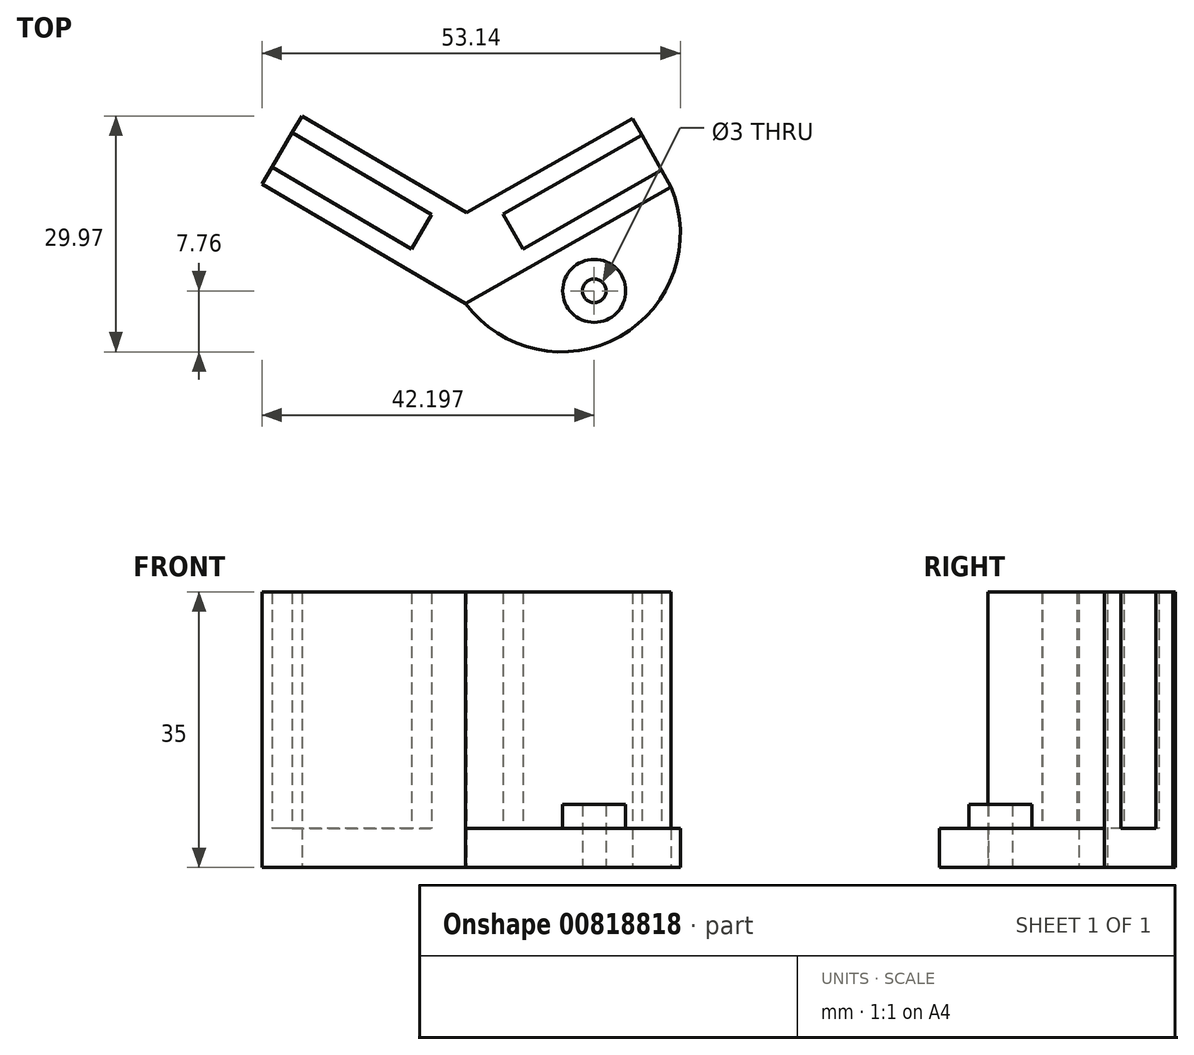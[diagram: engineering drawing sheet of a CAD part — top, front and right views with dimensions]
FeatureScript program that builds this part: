
annotation { "Feature Type Name" : "Feature", "Feature Type Description" : "" }
export const myFeature = defineFeature(function(context is Context, id is Id, definition is map)
    precondition{}
    {
        {
            var Q0;
            Q0=qCreatedBy(makeId("Top.planeOp"),FACE);
            var sketch = newSketch(context, id + "F0", { "sketchPlane" : qUnion([Q0])});
            skCircle(sketch, "E0.cCircle", {"center": v(0, 0) * mm, "radius": 30 * mm, "construction": true});
            skLineSegment(sketch, "E0.0", {"start": v(-26.1, -14.8) * mm, "end": v(-25.86, 15.2) * mm});
            skLineSegment(sketch, "E0.1", {"start": v(-25.86, 15.2) * mm, "end": v(0.23, 30) * mm});
            skLineSegment(sketch, "E0.2", {"start": v(0.23, 30) * mm, "end": v(26.1, 14.8) * mm});
            skLineSegment(sketch, "E0.3", {"start": v(26.1, 14.8) * mm, "end": v(25.86, -15.2) * mm});
            skLineSegment(sketch, "E0.4", {"start": v(25.86, -15.2) * mm, "end": v(-0.23, -30) * mm});
            skLineSegment(sketch, "E0.5", {"start": v(-0.23, -30) * mm, "end": v(-26.1, -14.8) * mm});
            skLineSegment(sketch, "E1", {"start": v(66.66, -58.3) * mm, "end": v(69.7, -53.13) * mm});
            skLineSegment(sketch, "E2.0", {"start": v(-0.14, -18.45) * mm, "end": v(-21.03, -6.18) * mm});
            skLineSegment(sketch, "E2.1", {"start": v(20.93, -6.5) * mm, "end": v(-0.14, -18.45) * mm});
            skLineSegment(sketch, "E3.0", {"start": v(-0.21, -27.17) * mm, "end": v(-24.86, -12.68) * mm});
            skLineSegment(sketch, "E3.1", {"start": v(24.65, -13.07) * mm, "end": v(-0.21, -27.17) * mm});
            skLineSegment(sketch, "E4", {"start": v(20.93, -6.5) * mm, "end": v(25.86, -15.2) * mm});
            skLineSegment(sketch, "E5", {"start": v(-21.03, -6.18) * mm, "end": v(-26.1, -14.8) * mm});
            skArc(sketch, "E6", {"start": v(-0.23, -30) * mm, "mid": v(19.38, -34.18) * mm, "end": v(25.86, -15.2) * mm});
            skLineSegment(sketch, "E7", {"start": v(19.38, -34.18) * mm, "end": v(12.81, -22.6) * mm});
            skCircle(sketch, "E8", {"center": v(16.1, -28.4) * mm, "radius": 4 * mm});
            skLineSegment(sketch, "E9", {"start": v(4.53, -18.62) * mm, "end": v(7.05, -23.05) * mm});
            skLineSegment(sketch, "E10", {"start": v(-22.27, -8.29) * mm, "end": v(-4.54, -18.7) * mm});
            skLineSegment(sketch, "E11", {"start": v(-4.54, -18.7) * mm, "end": v(-7.13, -23.1) * mm});
            skLineSegment(sketch, "E12", {"start": v(4.53, -18.62) * mm, "end": v(22.14, -8.63) * mm});
            skCircle(sketch, "E13", {"center": v(16.1, -28.4) * mm, "radius": 1.5 * mm});
            skSolve(sketch);
        }
        {
            var Q0;
            {var subQ7=sQuery(id+"F0.wireOp",EDGE,"E2.0");Q0=makeQuery(id+"F0.imprint","IMPRINT",FACE,{"disambiguationData":[TD([[makeQuery(id+"F0.imprint","IMPRINT",EDGE,{"derivedFrom":subQ7}),1.0]])]});}
            var Q1;
            {var subQ0=sQuery(id+"F0.wireOp",EDGE,"E0.5");Q1=makeQuery(id+"F0.imprint","IMPRINT",FACE,{"disambiguationData":[TD([[makeQuery(id+"F0.imprint","IMPRINT",EDGE,{"derivedFrom":subQ0}),-1.0]])]});}
            extrude(context, id + "F1", {"entities" : qUnion([Q0, Q1]), "depth" : 35 * mm, "offsetDistance" : 25 * mm});
        }
        {
            var Q0;
            {var subQ4=sQuery(id+"F0.wireOp",EDGE,"E10");Q0=makeQuery(id+"F0.imprint","IMPRINT",FACE,{"disambiguationData":[TD([[makeQuery(id+"F0.imprint","IMPRINT",EDGE,{"derivedFrom":subQ4}),-1.0]])]});}
            var Q1;
            {var subQ3=sQuery(id+"F0.wireOp",EDGE,"E9");Q1=makeQuery(id+"F0.imprint","IMPRINT",FACE,{"disambiguationData":[TD([[makeQuery(id+"F0.imprint","IMPRINT",EDGE,{"derivedFrom":subQ3}),1.0]])]});}
            extrude(context, id + "F2", {"entities" : qUnion([Q0, Q1]), "operationType" : NewBodyOperationType.ADD, "depth" : 5 * mm, "offsetDistance" : 25 * mm});
        }
        {
            var Q0;
            {var subQ0=sQuery(id+"F0.wireOp",EDGE,"E7");var subQ1=sQuery(id+"F0.wireOp",EDGE,"E6");var subQ2=makeQuery(id+"F0.imprint","INTERSECT",VERTEX,{"derivedFrom":[subQ1,subQ0]});Q0=makeQuery(id+"F0.imprint","IMPRINT",FACE,{"disambiguationData":[TD([[makeQuery(id+"F0.imprint","IMPRINT",EDGE,{"disambiguationData":[TD([[subQ2,-1.0]])],"derivedFrom":subQ0}),1.0]])]});}
            var Q1;
            {var subQ0=sQuery(id+"F0.wireOp",EDGE,"E7");var subQ1=sQuery(id+"F0.wireOp",EDGE,"E6");var subQ2=makeQuery(id+"F0.imprint","INTERSECT",VERTEX,{"derivedFrom":[subQ1,subQ0]});Q1=makeQuery(id+"F0.imprint","IMPRINT",FACE,{"disambiguationData":[TD([[makeQuery(id+"F0.imprint","IMPRINT",EDGE,{"disambiguationData":[TD([[subQ2,-1.0]])],"derivedFrom":subQ0}),-1.0]])]});}
            extrude(context, id + "F3", {"entities" : qUnion([Q0, Q1]), "operationType" : NewBodyOperationType.ADD, "depth" : 5 * mm, "offsetDistance" : 25 * mm});
        }
        {
            var Q0;
            {var subQ0=sQuery(id+"F0.wireOp",EDGE,"E8");var subQ1=sQuery(id+"F0.wireOp",EDGE,"E7");var subQ2=makeQuery(id+"F0.imprint","INTERSECT",VERTEX,{"disambiguationData":[OD(0.0)],"derivedFrom":[subQ1,subQ0]});Q0=makeQuery(id+"F0.imprint","IMPRINT",FACE,{"disambiguationData":[TD([[makeQuery(id+"F0.imprint","IMPRINT",EDGE,{"disambiguationData":[TD([[subQ2,-1.0]])],"derivedFrom":subQ1}),1.0]])]});}
            var Q1;
            {var subQ0=sQuery(id+"F0.wireOp",EDGE,"E8");var subQ1=sQuery(id+"F0.wireOp",EDGE,"E7");var subQ2=makeQuery(id+"F0.imprint","INTERSECT",VERTEX,{"disambiguationData":[OD(0.0)],"derivedFrom":[subQ1,subQ0]});Q1=makeQuery(id+"F0.imprint","IMPRINT",FACE,{"disambiguationData":[TD([[makeQuery(id+"F0.imprint","IMPRINT",EDGE,{"disambiguationData":[TD([[subQ2,-1.0]])],"derivedFrom":subQ1}),-1.0]])]});}
            extrude(context, id + "F4", {"entities" : qUnion([Q0, Q1]), "operationType" : NewBodyOperationType.ADD, "depth" : 8 * mm, "offsetDistance" : 25 * mm});
        }
    });
